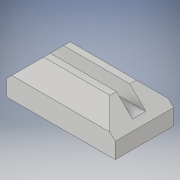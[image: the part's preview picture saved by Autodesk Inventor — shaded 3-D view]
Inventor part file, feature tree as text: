
AUTODESK INVENTOR PART (.ipt)
format: ipt  version: 2019 (Build 230136000, 136)  size: 117,760 bytes
history: native  units: in
note: dims shown in document units (in); Inventor stores cm internally (conversion verified against a paired STEP export)
features: extrude x2, chamfer x2, sketch x2
ambient origin geometry x8: Origin, YZ Plane, XZ Plane, XY Plane, X Axis, Y Axis, Z Axis, Center Point
bodies: Solid1 (feature_tree)
feature tree (6):
  extrude  "Extrusion1"  Depth=2.75in
  extrude  "Extrusion2"  Depth=0.75in
  chamfer  "Chamfer1"  Distance=0.625in
  chamfer  "Chamfer2"  Distance=0.75in
  sketch  "Sketch1"  dims[d0=5.125in d1=2.75in]
  sketch  "Sketch2"  dims[d2=1.75in d3=0.0in d4=0.3125in d5=0.625in d6=0.75in d7=0.0in d8=1.0in d9=0.125in d10=45.0deg d11=0.75in d12=0.125in d13=45.0deg]
